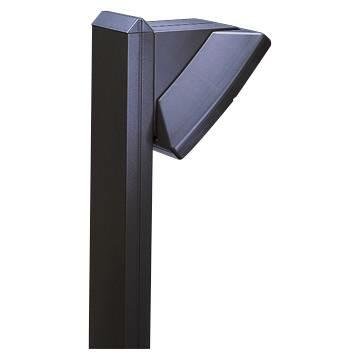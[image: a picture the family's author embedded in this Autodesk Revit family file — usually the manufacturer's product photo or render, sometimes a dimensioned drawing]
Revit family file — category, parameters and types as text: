
# Revit family: Lighting-UrbanLighting-GEWISS-EXTRO-SINGLE_SUPPORT
name_source: partatom
category: Apparecchi per illuminazione
units: mm (PartAtom-declared; Revit-internal decimal feet)

## family parameters
Basato su piano di lavoro = Sì
Condiviso = No
Numero OmniClass = 23.80.00.00
Punto di calcolo locali = Sì
Quota connettore circolare = Usa diametro
Sempre verticale = Sì
Sorgente d'illuminazione = No
Taglio con vuoti quando caricato = No
Tipo di parte = Normale
Titolo OmniClass = Electric Power and Lighting

## types (1)
- GW82292 - EXTRO SINGLE COLUMN H.1300 G.GREY
    Altezza colonna = 1300 mm  [stored 4.26509 ft]
    Catalogue = LIGHTING
    Catalogue Range = EXTRO
    Colonna = GEWISS - Grigio Graffite
    Colour = Graphite grey
    Descrizione = EXTRO SINGLE COLUMN H.1300 G.GREY
    EAN code = 8011564210387
    Electrocod = 240
    Height (mm) = 1300
    IDF = fec547e4-50c5-42fa-8bc7-d93a754f0462
    IDT = edb79119-9e68-4dab-b5a6-da154a75fe80
    Immagine tipo = GW82259.jpg
    Larghezza colonna = 60 mm  [stored 0.19685 ft]
    Lunghezza colonna = 140 mm  [stored 0.459318 ft]
    Material = Extruded aluminium
    Modello = GW82292
    Planting (m) = 0.25
    Planting recommended = 250MM
    Produttore = GEWISS S.p.A.
    Prospetto di default = 1219 mm
    SEO = Column
    Tappo colonna = <Per categoria>
    Technical sheet = https://www.gewiss.com
    URL = https://www.gewiss.com
    Version file RFA = 20.11

note: [stored X ft] marks values corroborated as IEEE doubles in the binary element streams (Revit-internal decimal feet)
